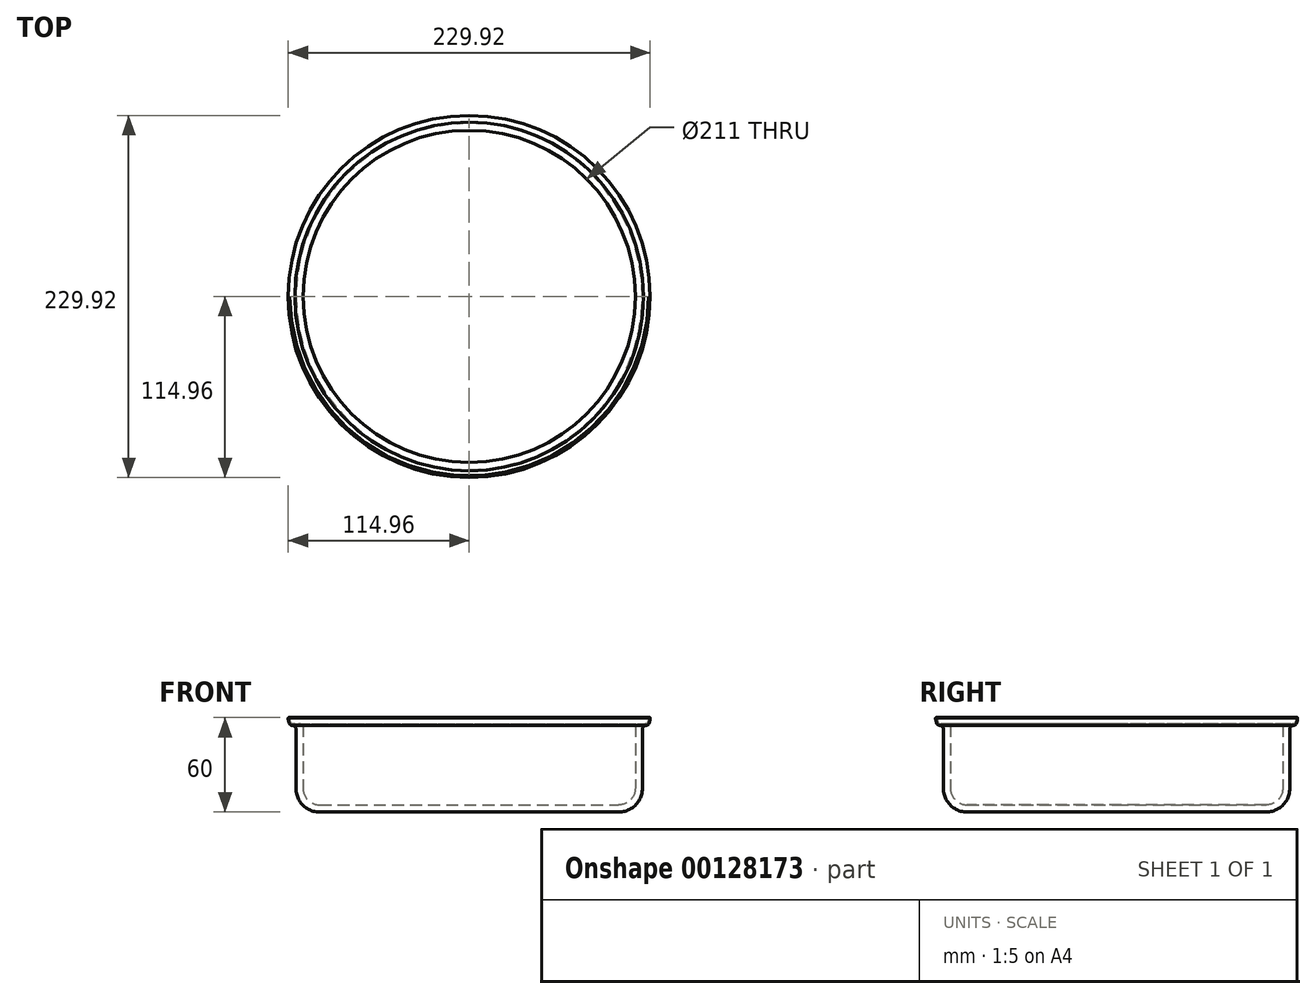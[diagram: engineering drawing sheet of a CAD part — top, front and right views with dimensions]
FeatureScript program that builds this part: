
annotation { "Feature Type Name" : "Feature", "Feature Type Description" : "" }
export const myFeature = defineFeature(function(context is Context, id is Id, definition is map)
    precondition{}
    {
        {
            var Q0;
            Q0=qCreatedBy(makeId("Front.planeOp"),FACE);
            var sketch = newSketch(context, id + "F0", { "sketchPlane" : qUnion([Q0])});
            skLineSegment(sketch, "E0", {"start": v(110, 15) * mm, "end": v(110, 52.53) * mm});
            skLineSegment(sketch, "E1.top", {"start": v(112.4, 55.03) * mm, "end": v(112.5, 55.03) * mm});
            skPoint(sketch, "E2.visualSharp", {"position": v(110, 0) * mm});
            skArc(sketch, "E2.filletArc", {"start": v(95, 0) * mm, "mid": v(105.6, 4.4) * mm, "end": v(110, 15) * mm});
            skFitSpline(sketch, "E3", {"points": [v(110, 55.03) * mm, v(112.4, 55.03) * mm, v(114.96, 59.82) * mm], "startDerivative": vector(9.38, 0) * mm, "endDerivative": vector(1.32, 21.66) * mm});
            skPoint(sketch, "E4.orphan", {"position": v(110, 60) * mm});
            skPoint(sketch, "E5.orphan", {"position": v(114.8, 55.03) * mm});
            skArc(sketch, "E6.filletArc", {"start": v(112.5, 55.03) * mm, "mid": v(110.73, 54.3) * mm, "end": v(110, 52.53) * mm});
            skFitSpline(sketch, "E7.0", {"points": [v(110, 56.03) * mm, v(110.4, 56.03) * mm, v(111.05, 56.02) * mm, v(111.61, 56) * mm, v(111.96, 56) * mm, v(112.16, 56.01) * mm, v(112.33, 56.03) * mm, v(112.5, 56.05) * mm, v(112.66, 56.08) * mm, v(112.8, 56.13) * mm, v(112.95, 56.22) * mm, v(113.1, 56.37) * mm, v(113.3, 56.65) * mm, v(113.5, 57.1) * mm, v(113.76, 58) * mm, v(113.9, 59.02) * mm, v(113.96, 59.88) * mm]});
            skArc(sketch, "E8.0", {"start": v(95, 4.5) * mm, "mid": v(102.42, 7.58) * mm, "end": v(105.5, 15) * mm});
            skPoint(sketch, "E9", {"position": v(107.92, 54.5) * mm});
            skArc(sketch, "E10", {"start": v(114.96, 59.82) * mm, "mid": v(114.47, 60) * mm, "end": v(113.96, 59.88) * mm});
            skPoint(sketch, "E10.second.point", {"position": v(114.8, 58.29) * mm});
            skLineSegment(sketch, "E11.trimOffspring", {"start": v(113.8, 58.43) * mm, "end": v(113.8, 58.43) * mm});
            skLineSegment(sketch, "E12", {"start": v(112.3, 56.03) * mm, "end": v(108.4, 56.03) * mm});
            skPoint(sketch, "E13.visualSharp", {"position": v(105.5, 56.03) * mm});
            skArc(sketch, "E13.filletArc", {"start": v(108.4, 56.03) * mm, "mid": v(106.88, 55.79) * mm, "end": v(105.5, 55.1) * mm});
            skLineSegment(sketch, "E14", {"start": v(0, 0) * mm, "end": v(0, 4.5) * mm});
            skLineSegment(sketch, "E15", {"start": v(105.5, 15) * mm, "end": v(105.5, 55.1) * mm});
            skLineSegment(sketch, "E16.bottom", {"start": v(0, 4.5) * mm, "end": v(92.42, 4.5) * mm});
            skLineSegment(sketch, "E16.top", {"start": v(0, 0) * mm, "end": v(92.42, 0) * mm});
            skLineSegment(sketch, "E16.left", {"start": v(0, 4.5) * mm, "end": v(0, 0) * mm});
            skLineSegment(sketch, "E17", {"start": v(92.42, 0) * mm, "end": v(95, 0) * mm});
            skLineSegment(sketch, "E18", {"start": v(92.42, 4.5) * mm, "end": v(95, 4.5) * mm});
            skPoint(sketch, "E19", {"position": v(110, 33.77) * mm});
            skSolve(sketch);
        }
        {
            var Q0;
            Q0=makeQuery(id+"F0.imprint","IMPRINT",FACE,{"disambiguationData":[TD([[makeQuery(id+"F0.imprint","IMPRINT",EDGE,{"derivedFrom":sQuery(id+"F0.wireOp",EDGE,"E0")}),1.0]])]});
            var Q1;
            Q1=sQuery(id+"F0.wireOp",EDGE,"E14");
            revolve(context, id + "F1", {"entities" : qUnion([Q0]), "axis" : qUnion([Q1]), "revolveType" : RevolveType.FULL});
        }
        {
            var Q0;
            Q0=sQuery(id+"F0.wireOp",EDGE,"E0");
            cPlane(context, id + "F2", {"entities" : qUnion([Q0]), "cplaneType" : CPlaneType.LINE_ANGLE, "offset" : 0 * mm, "angle" : 0 * degree, "width" : 150 * mm, "height" : 150 * mm});
        }
    });
